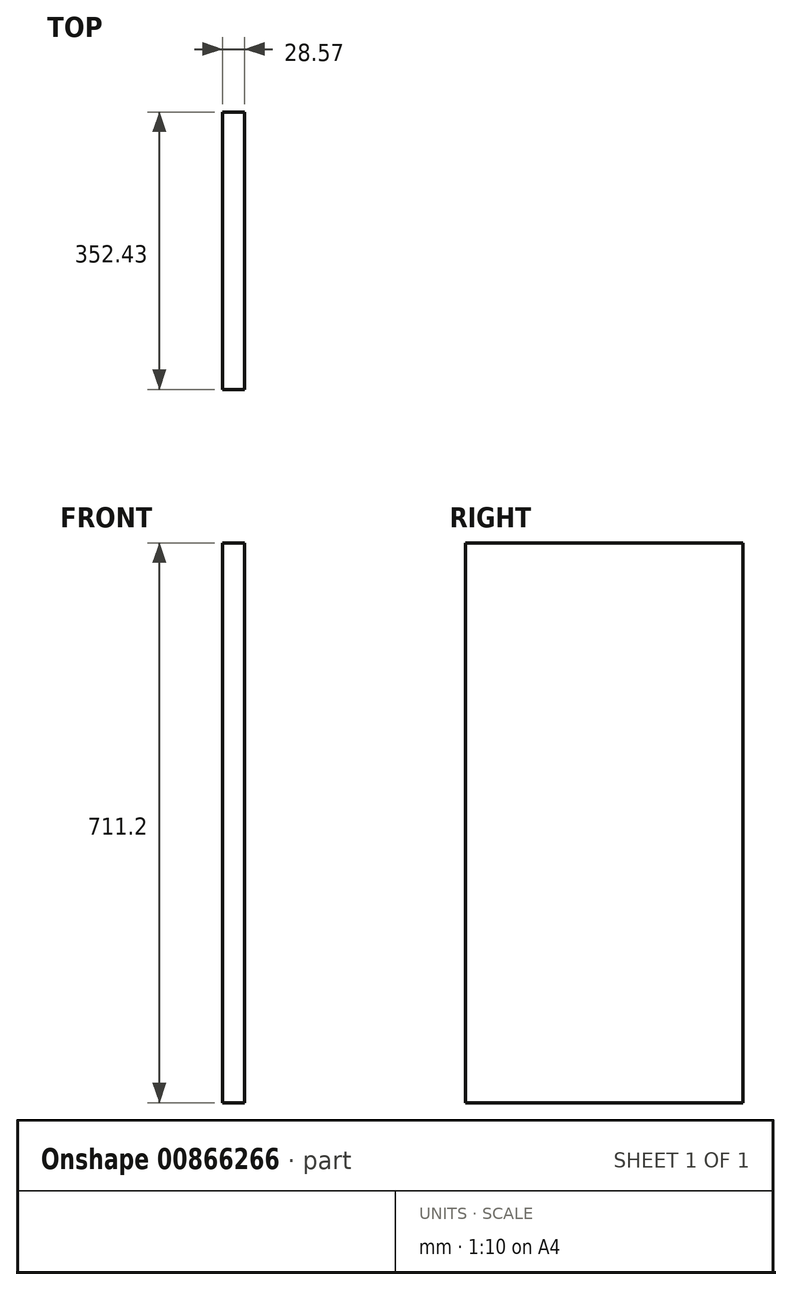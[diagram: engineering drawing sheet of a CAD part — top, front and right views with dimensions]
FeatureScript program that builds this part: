
annotation { "Feature Type Name" : "Feature", "Feature Type Description" : "" }
export const myFeature = defineFeature(function(context is Context, id is Id, definition is map)
    precondition{}
    {
        {
            var Q0;
            Q0=qCreatedBy(makeId("Right.planeOp"),FACE);
            var sketch = newSketch(context, id + "F0", { "sketchPlane" : qUnion([Q0])});
            skLineSegment(sketch, "E0.bottom", {"start": v(324.65, 674.9) * mm, "end": v(-27.78, 674.9) * mm});
            skLineSegment(sketch, "E0.top", {"start": v(324.65, -36.3) * mm, "end": v(-27.78, -36.3) * mm});
            skLineSegment(sketch, "E0.left", {"start": v(324.65, 674.9) * mm, "end": v(324.65, -36.3) * mm});
            skLineSegment(sketch, "E0.right", {"start": v(-27.78, 674.9) * mm, "end": v(-27.78, -36.3) * mm});
            skPoint(sketch, "E0.middle", {"position": v(148.44, 319.3) * mm});
            skSolve(sketch);
        }
        {
            var Q0;
            Q0=makeQuery(id+"F0.imprint","IMPRINT",FACE,{"disambiguationData":[TD([[makeQuery(id+"F0.imprint","IMPRINT",EDGE,{"derivedFrom":sQuery(id+"F0.wireOp",EDGE,"E0.bottom")}),1.0]])]});
            extrude(context, id + "F1", {"entities" : qUnion([Q0]), "depth" : 28.57 * mm, "offsetDistance" : 25.4 * mm});
        }
    });
